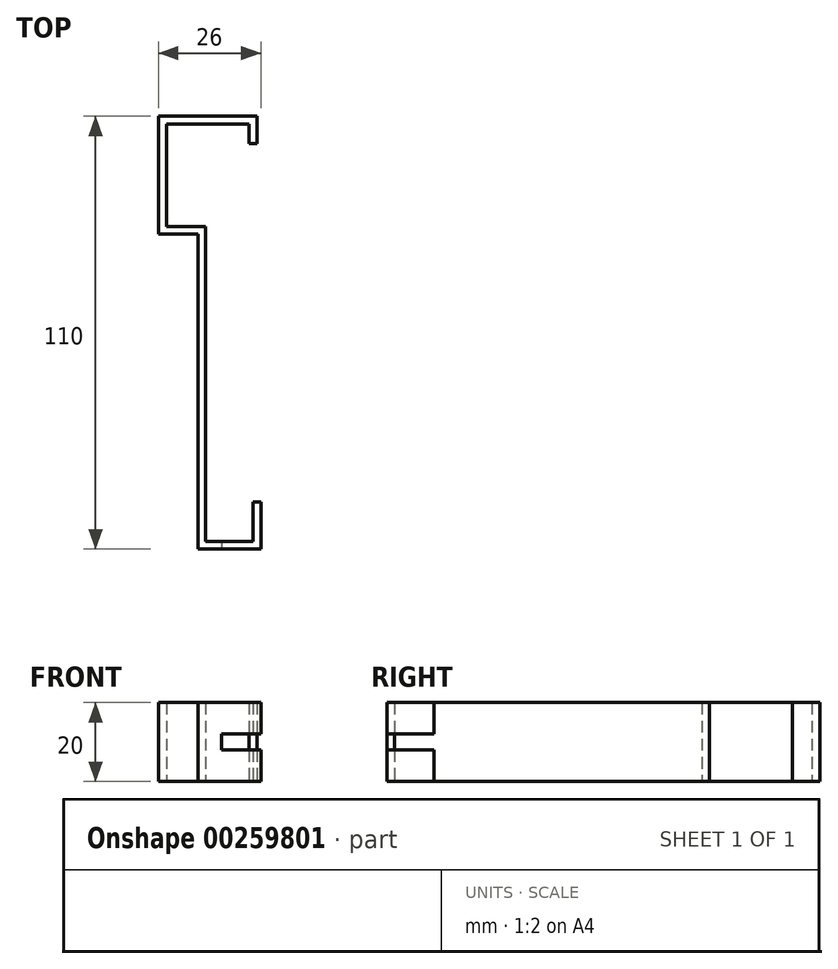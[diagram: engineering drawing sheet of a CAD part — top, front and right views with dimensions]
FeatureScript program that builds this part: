
annotation { "Feature Type Name" : "Feature", "Feature Type Description" : "" }
export const myFeature = defineFeature(function(context is Context, id is Id, definition is map)
    precondition{}
    {
        {
            var Q0;
            Q0=qCreatedBy(makeId("Top.planeOp"),FACE);
            var sketch = newSketch(context, id + "F0", { "sketchPlane" : qUnion([Q0])});
            skLineSegment(sketch, "E0", {"start": v(3.16, 34.7) * mm, "end": v(3.16, 39.7) * mm});
            skLineSegment(sketch, "E1", {"start": v(3.16, 39.7) * mm, "end": v(-17.84, 39.7) * mm});
            skLineSegment(sketch, "E2", {"start": v(-17.84, 39.7) * mm, "end": v(-17.84, 13.7) * mm});
            skLineSegment(sketch, "E3", {"start": v(-17.84, 13.7) * mm, "end": v(-7.84, 13.7) * mm});
            skLineSegment(sketch, "E4", {"start": v(-7.84, 13.7) * mm, "end": v(-7.84, -66.3) * mm});
            skLineSegment(sketch, "E5", {"start": v(-7.84, -66.3) * mm, "end": v(4.16, -66.3) * mm});
            skLineSegment(sketch, "E6", {"start": v(4.16, -66.3) * mm, "end": v(4.16, -56.3) * mm});
            skLineSegment(sketch, "E7.0", {"start": v(6.16, -68.3) * mm, "end": v(6.16, -56.3) * mm});
            skLineSegment(sketch, "E7.1", {"start": v(-9.84, -68.3) * mm, "end": v(6.16, -68.3) * mm});
            skLineSegment(sketch, "E7.2", {"start": v(-9.84, 11.7) * mm, "end": v(-9.84, -68.3) * mm});
            skLineSegment(sketch, "E7.4", {"start": v(5.16, 41.7) * mm, "end": v(-19.84, 41.7) * mm});
            skLineSegment(sketch, "E7.5", {"start": v(-19.84, 41.7) * mm, "end": v(-19.84, 11.7) * mm});
            skLineSegment(sketch, "E7.6", {"start": v(-19.84, 11.7) * mm, "end": v(-9.84, 11.7) * mm});
            skLineSegment(sketch, "E8", {"start": v(5.16, 41.7) * mm, "end": v(5.16, 34.7) * mm});
            skLineSegment(sketch, "E9", {"start": v(5.16, 34.7) * mm, "end": v(3.16, 34.7) * mm});
            skLineSegment(sketch, "E10", {"start": v(4.16, -56.3) * mm, "end": v(6.16, -56.3) * mm});
            skSolve(sketch);
        }
        {
            var Q0;
            Q0=makeQuery(id+"F0.imprint","IMPRINT",FACE,{"disambiguationData":[TD([[makeQuery(id+"F0.imprint","IMPRINT",EDGE,{"derivedFrom":sQuery(id+"F0.wireOp",EDGE,"E0")}),-1.0]])]});
            extrude(context, id + "F1", {"entities" : qUnion([Q0]), "depth" : 20 * mm, "offsetDistance" : 25 * mm});
        }
        {
            var Q0;
            Q0=makeQuery(id+"F1.opExtrude","SWEPT_FACE",FACE,{"disambiguationData":[OSD([sQuery(id+"F0.wireOp",EDGE,"E7.0")])]});
            var sketch = newSketch(context, id + "F2", { "sketchPlane" : qUnion([Q0])});
            skLineSegment(sketch, "E11", {"start": v(-56.3, 12) * mm, "end": v(-68.3, 12) * mm});
            skLineSegment(sketch, "E12", {"start": v(-68.3, 12) * mm, "end": v(-68.3, 8) * mm});
            skLineSegment(sketch, "E13", {"start": v(-68.3, 8) * mm, "end": v(-56.3, 8) * mm});
            skSolve(sketch);
        }
        {
            var Q0;
            {var subQ0=sQuery(id+"F2.wireOp",EDGE,"E11");Q0=makeQuery(id+"F2.imprint","IMPRINT",FACE,{"disambiguationData":[TD([[makeQuery(id+"F2.imprint","IMPRINT",EDGE,{"derivedFrom":subQ0}),1.0]])]});}
            extrude(context, id + "F3", {"entities" : qUnion([Q0]), "operationType" : NewBodyOperationType.REMOVE, "oppositeDirection" : true, "depth" : 10 * mm, "offsetDistance" : 25 * mm});
        }
    });
